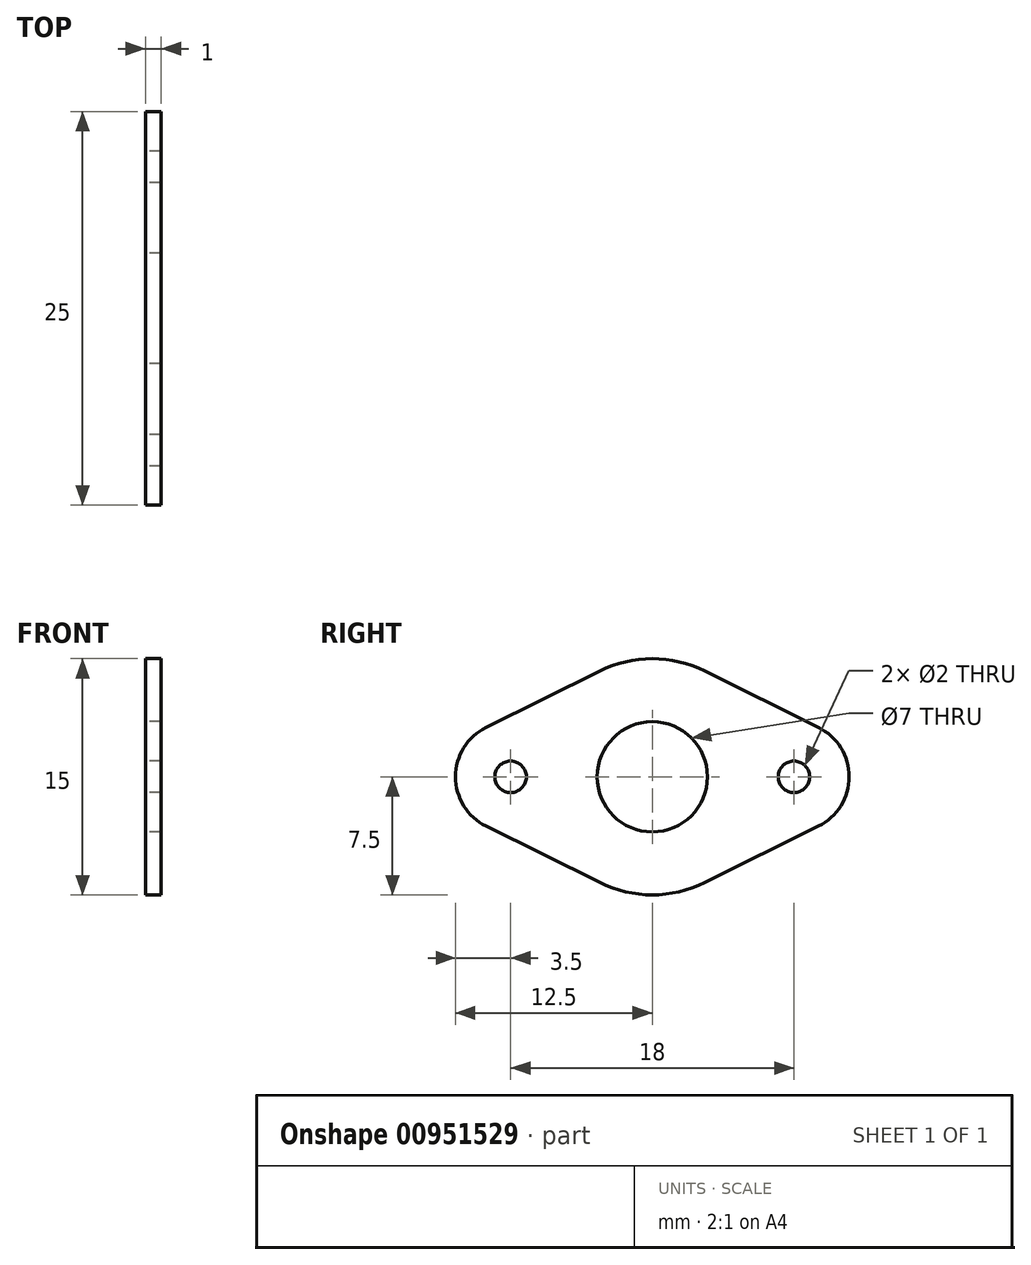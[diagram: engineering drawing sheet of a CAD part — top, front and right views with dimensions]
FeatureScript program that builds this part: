
annotation { "Feature Type Name" : "Feature", "Feature Type Description" : "" }
export const myFeature = defineFeature(function(context is Context, id is Id, definition is map)
    precondition{}
    {
        {
            var Q0;
            Q0=qCreatedBy(makeId("Right.planeOp"),FACE);
            var sketch = newSketch(context, id + "F0", { "sketchPlane" : qUnion([Q0])});
            skCircle(sketch, "E0", {"center": v(0, 0) * mm, "radius": 3.5 * mm});
            skCircle(sketch, "E1", {"center": v(9, 0) * mm, "radius": 3.5 * mm});
            skCircle(sketch, "E2", {"center": v(-9, 0) * mm, "radius": 1 * mm});
            skCircle(sketch, "E3", {"center": v(0, 0) * mm, "radius": 7.5 * mm});
            skCircle(sketch, "E4", {"center": v(-9, 0) * mm, "radius": 3.5 * mm});
            skCircle(sketch, "E5", {"center": v(9, 0) * mm, "radius": 1 * mm});
            skLineSegment(sketch, "E6", {"start": v(-10.56, 3.14) * mm, "end": v(-3.33, 6.72) * mm});
            skLineSegment(sketch, "E7", {"start": v(3.33, 6.72) * mm, "end": v(10.56, 3.14) * mm});
            skLineSegment(sketch, "E8", {"start": v(10.56, -3.14) * mm, "end": v(3.33, -6.72) * mm});
            skLineSegment(sketch, "E9", {"start": v(-10.56, -3.14) * mm, "end": v(-3.33, -6.72) * mm});
            skSolve(sketch);
        }
        {
            var Q0;
            Q0 = qSketchRegion(id + "F0", true);
            var Q1;
            {var subQ0=sQuery(id+"F0.wireOp",EDGE,"E4");var subQ1=sQuery(id+"F0.wireOp",EDGE,"E3");var subQ2=makeQuery(id+"F0.imprint","INTERSECT",VERTEX,{"disambiguationData":[OD(0.0)],"derivedFrom":[subQ1,subQ0]});Q1=makeQuery(id+"F0.imprint","IMPRINT",FACE,{"disambiguationData":[TD([[makeQuery(id+"F0.imprint","IMPRINT",EDGE,{"disambiguationData":[TD([[subQ2,-1.0]])],"derivedFrom":subQ1}),1.0]])]});}
            var Q2;
            {var subQ0=sQuery(id+"F0.wireOp",EDGE,"E3");var subQ1=sQuery(id+"F0.wireOp",EDGE,"E1");var subQ2=makeQuery(id+"F0.imprint","INTERSECT",VERTEX,{"disambiguationData":[OD(0.0)],"derivedFrom":[subQ1,subQ0]});Q2=makeQuery(id+"F0.imprint","IMPRINT",FACE,{"disambiguationData":[TD([[makeQuery(id+"F0.imprint","IMPRINT",EDGE,{"disambiguationData":[TD([[subQ2,-1.0]])],"derivedFrom":subQ1}),1.0]])]});}
            extrude(context, id + "F1", {"entities" : qUnion([Q0, Q1, Q2]), "depth" : 1 * mm, "offsetDistance" : 25 * mm});
        }
    });
